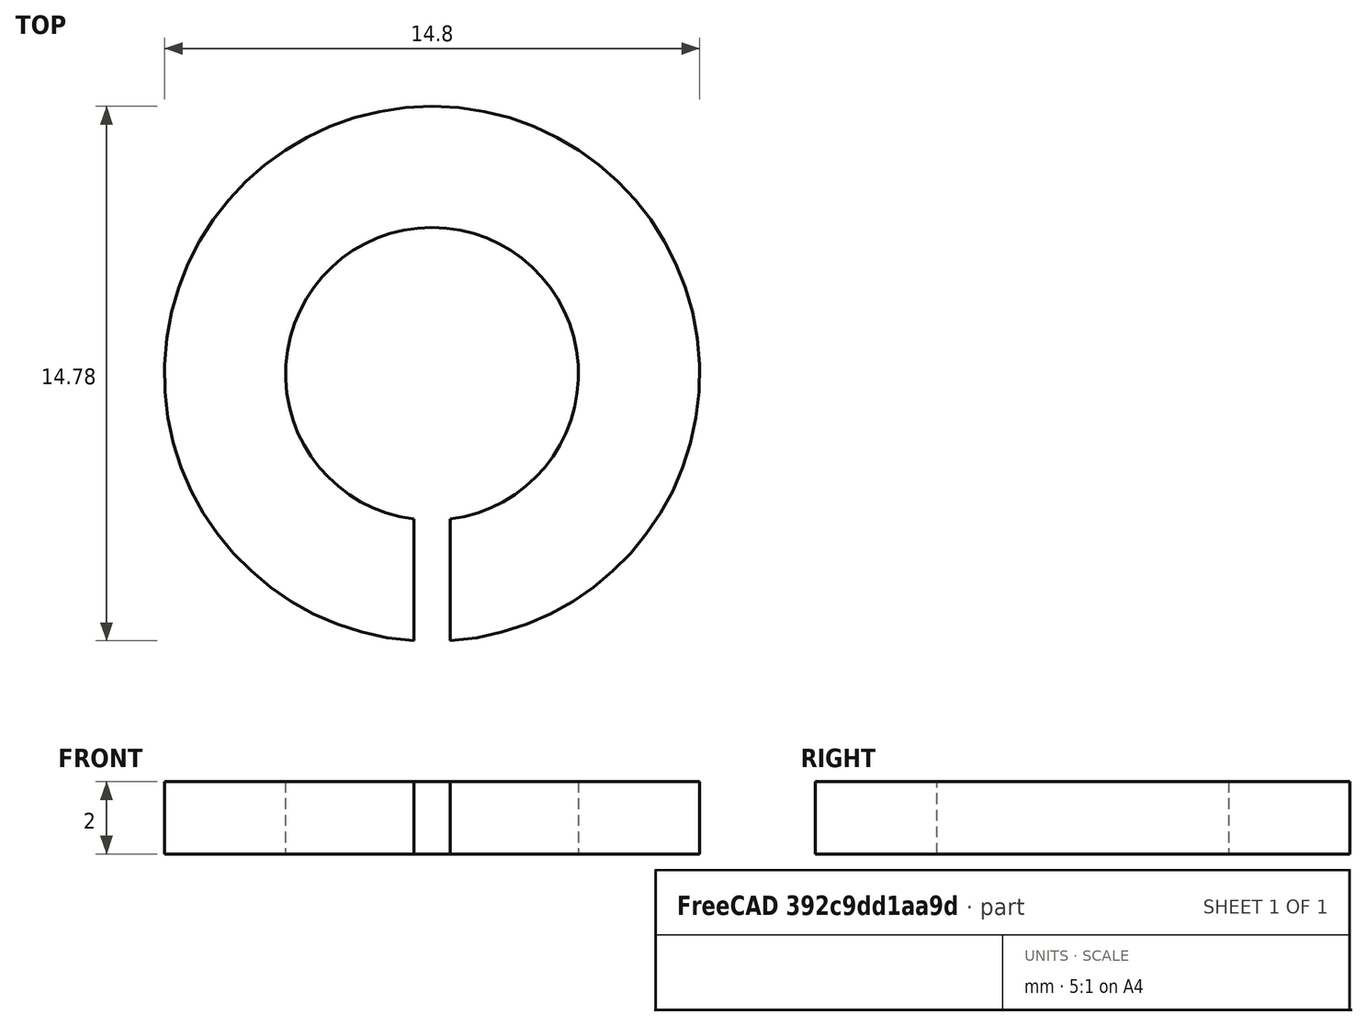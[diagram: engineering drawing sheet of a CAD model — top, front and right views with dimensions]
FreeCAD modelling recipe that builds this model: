
FCSTD DOCUMENT  (FreeCAD 0.15R4651 (Git))
Label: Federring_DIN127-B8
License: All rights reserved
LicenseURL: http://de.wikipedia.org/wiki/Alle_Rechte_vorbehalten
objects: Sketcher::SketchObject×1, PartDesign::Pad×1
note: 3 computed .brp shape members not serialized (recipe doc carries the construction recipe); baked Part::Feature solids carry a one-line shape summary decoded from their .brp

FEATURE [Sketcher::SketchObject] Sketch
  sketch-geometry (4):
    g0: ArcOfCircle CenterX=0 CenterY=0 CenterZ=0 NormalX=0 NormalY=0 NormalZ=1 Radius=4.05 StartAngle=4.83616 EndAngle=10.8718
    g1: ArcOfCircle CenterX=0 CenterY=0 CenterZ=0 NormalX=0 NormalY=0 NormalZ=1 Radius=7.4 StartAngle=4.78001 EndAngle=10.928
    g2: LineSegment StartX=0.5 StartY=-4.01902 StartZ=0 EndX=0.5 EndY=-7.38309 EndZ=0
    g3: LineSegment StartX=-0.5 StartY=-7.38309 StartZ=0 EndX=-0.5 EndY=-4.01902 EndZ=0
  constraints (12):
    c: Coincident(g0,g-1)
    c: Coincident(g1,g-1)
    c: Vertical(g2)
    c: Vertical(g3)
    c: Coincident(g0,g2)
    c: Coincident(g0,g3)
    c: Coincident(g1,g2)
    c: Coincident(g1,g3)
    c: Symmetric(g1,g1,g-2)
    c: Radius(g0) = 4.05
    c: Radius(g1) = 7.4
    c: DistanceX(g1,g1) = -1
FEATURE [PartDesign::Pad] Pad  label="Federring DIN 127-B 8 #"
  Length = 2
  Length2 = 100
  Midplane = true
  Sketch = -> Sketch
  Type = 0
